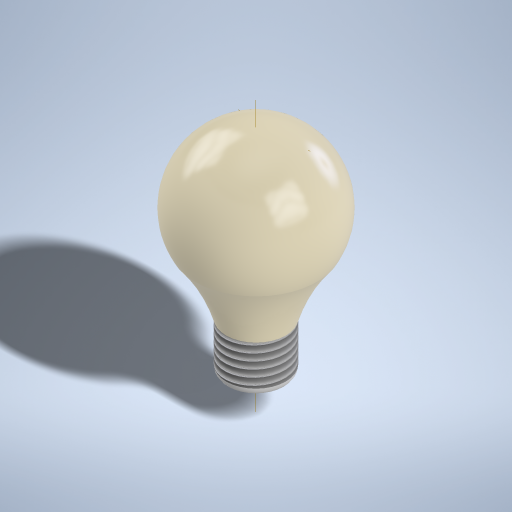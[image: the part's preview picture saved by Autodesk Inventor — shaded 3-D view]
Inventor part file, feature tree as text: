
AUTODESK INVENTOR PART (.ipt)
format: ipt  version: 2023 (Build 270158000, 158)  size: 1,043,456 bytes
history: native  units: mm
features: sketch x12, extrude x8, fillet x3, thread x2, hole x2, other x2, revolve x1, chamfer x1, pattern_circular x1, pattern_linear x1, helix x1, mirror x1
ambient origin geometry x8: Origin, YZ Plane, XZ Plane, XY Plane, X Axis, Y Axis, Z Axis, Center Point
bodies: Solid1 (feature_tree)
feature tree (35):
  extrude  "Extrusion1"  Depth=15.0mm TaperAngle=0.0deg
  revolve  "Revolution2"  [1 undecoded]
  fillet  "Fillet2"  [1 undecoded]
  extrude  "Extrusion2"  Depth=4.0mm
  chamfer  "Chamfer1"  Distance=5.0mm
  thread  "Thread3"  [1 undecoded]
  extrude  "Extrusion3"  Depth=4.0mm
  extrude  "Extrusion4"  Depth=1.0mm
  extrude  "Extrusion5"  Depth=4.0mm
  fillet  "Fillet4"  Radius=15.0mm
  extrude  "Extrusion6"  Depth=2.0mm
  hole  "Hole3"  [1 undecoded]
  thread  "Thread4"  [1 undecoded]
  hole  "Hole5"  [1 undecoded]
  other  "Work Axis7"
  pattern_circular  "Circular Pattern2"  Count=2  [1 undecoded]
  pattern_linear  "Rectangular Pattern2"  Spacing1=3.0mm  [1 undecoded]
  extrude  "Extrusion7"  Depth=10.0mm TaperAngle=0.0deg
  extrude  "Extrusion9"  Depth=10.0mm
  fillet  "Fillet5"  Radius=17.5mm
  other  "Work Axis11"
  helix  "Coil1"  [1 undecoded]
  mirror  "Mirror1"
  sketch  "Sketch1"  dims[d0=15.0mm d1=15.0mm d2=0.0mm]
  sketch  "Sketch2"  dims[d4=35.0mm d7=50.0mm d20=180.0deg]
  sketch  "Sketch4"  dims[d24=5.0mm d25=0.0mm d28=4.0mm]
  sketch  "Sketch5"  dims[d29=9.0mm d30=5.0mm d31=0.0mm d33=5.0mm d34=5.0mm d35=45.0deg]
  sketch  "Sketch6"  dims[d36=16.0mm d37=0.0mm d38=4.0mm]
  sketch  "Sketch7"  dims[d41=3.904952mm d42=1.0mm]
  sketch  "Sketch8"  dims[d43=1.0mm d44=4.0mm d45=15.0mm d46=0.0mm]
  sketch  "Sketch10"  dims[d47=8.0mm d48=2.0mm]
  sketch  "Sketch11"  dims[d49=0.0mm d50=0.0mm d51=10.0mm d52=1.0mm d53=0.0mm]
  sketch  "Sketch12"  dims[d54=0.4mm d59=45.0mm]
  sketch  "Sketch17"  dims[d60=3.490659mm d61=20.0mm]
  sketch  "Sketch22"  dims[d62=1.0mm d63=0.0mm d78=3.0mm d86=1.778mm d87=3.708mm d88=3.023mm d89=2.0mm d90=14.3117mm d91=5.0mm d92=0.0mm d93=19.85mm d94=0.0mm d95=2.5mm d104=17.5mm d105=1.0mm d106=6.0mm d107=4.0mm d108=2.0mm d109=90.0deg d110=8.0mm d111=20.594885mm d112=60.0mm d113=7.504916mm d115=80.0mm d117=40.0mm d122=15.0mm d123=0.1mm d124=1.5mm d125=0.0mm d132=1.0mm d136=0.1mm d137=8.0mm d138=4.5mm d139=60.0mm d140=0.0mm d141=90.0deg d142=90.0deg d143=0.0mm d144=0.0mm d145=40.0mm d147=5.0mm d148=10.0mm d150=10.0mm d152=1.0mm d153=1.5mm d154=1.0mm d155=0.5mm d156=0.0mm d158=40.0mm d160=10.0mm d161=1.0mm d162=1.5mm d163=1.0mm d165=40.0mm d167=10.0mm d168=1.0mm d169=1.5mm d170=1.0mm d172=40.0mm d174=10.0mm d175=1.0mm d176=1.5mm d177=1.0mm d26=0.5mm d27=0.872665mm d118=0.0mm d119=0.0mm d120=0.0mm d121=0.0mm d133=0.0mm d134=0.0mm d135=0.0mm]
note: 9 required parameter values undecoded (feature->parameter linkage not recoverable at this tier; creation-order binding heuristic only, values carry confidence <= 0.55)